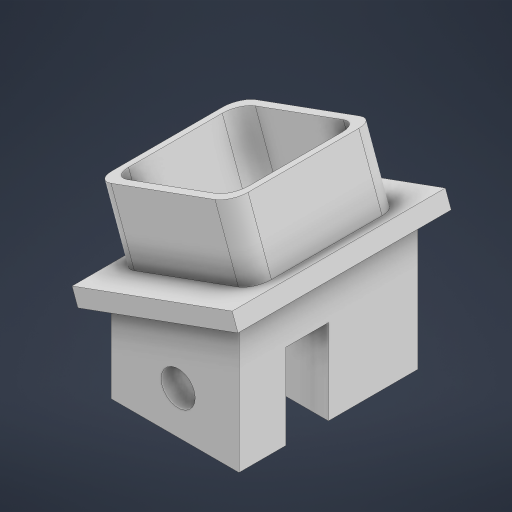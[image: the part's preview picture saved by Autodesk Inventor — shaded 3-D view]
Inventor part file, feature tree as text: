
AUTODESK INVENTOR PART (.ipt)
format: ipt  version: 2024 (Build 280153000, 153)  size: 262,144 bytes
history: native  units: mm
features: reference x11, extrude x5, sketch x5, other x4, fillet x1, projected_geometry x1
ambient origin geometry x8: Origin, YZ Plane, XZ Plane, XY Plane, X Axis, Y Axis, Z Axis, Center Point
bodies: Body1 (feature_tree)
feature tree (27):
  other  "Твердое тело1"
  extrude  "Выдавливание1"  Depth=10.0mm TaperAngle=0.0deg
  extrude  "Выдавливание2"  Depth=10.0mm TaperAngle=0.0deg
  extrude  "Выдавливание3"  Depth=3.490659mm
  extrude  "Выдавливание4"  Depth=10.0mm TaperAngle=0.0deg
  extrude  "Выдавливание5"  Depth=20.0mm
  fillet  "Сопряжение1"  Radius=2.0mm
  sketch  "Эскиз1"
  reference  "Ссылка1"
  reference  "Ссылка2"
  reference  "Ссылка3"
  reference  "Ссылка4"
  reference  "Ссылка5"
  reference  "Ссылка6"
  reference  "Ссылка7"
  reference  "Ссылка8"
  reference  "Ссылка16"
  reference  "Ссылка17"
  sketch  "Эскиз2"
  reference  "Ссылка18"
  sketch  "Эскиз3"
  sketch  "Эскиз4"
  projected_geometry  "Спроецированная петля1"
  sketch  "Эскиз5"
  parser-record x1  (decoder bookkeeping rows leaked as tree rows — omitted from the tree; the rows remain in map.json)
  other  "cum_holder_asembly.iam"
  other  "cum_holder_up:1"
note: 1 file-system path scrubbed to <path> (originals preserved in map.json)
